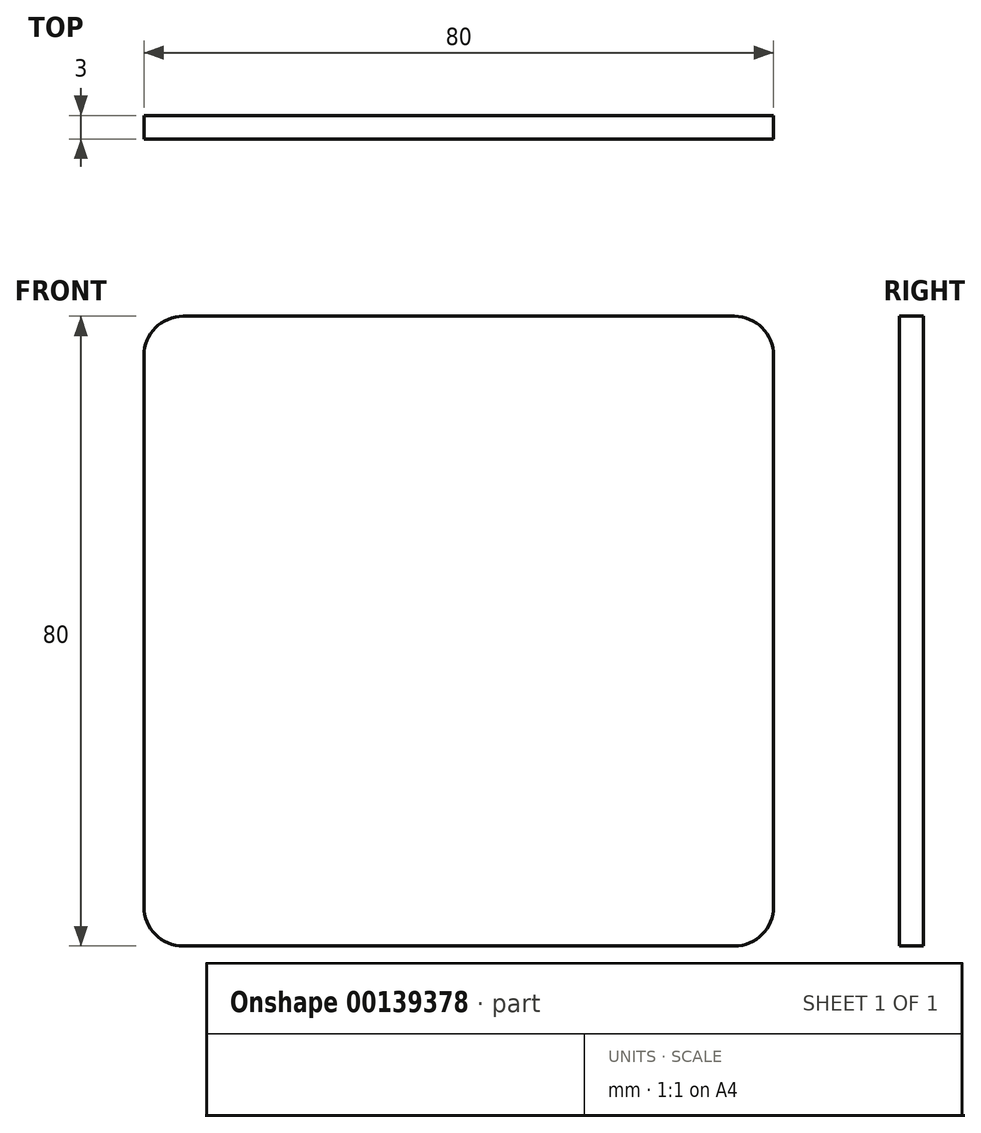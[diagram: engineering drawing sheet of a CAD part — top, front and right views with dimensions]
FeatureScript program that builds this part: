
annotation { "Feature Type Name" : "Feature", "Feature Type Description" : "" }
export const myFeature = defineFeature(function(context is Context, id is Id, definition is map)
    precondition{}
    {
        {
            var Q0;
            Q0=qCreatedBy(makeId("Front.planeOp"),FACE);
            var sketch = newSketch(context, id + "F0", { "sketchPlane" : qUnion([Q0])});
            skLineSegment(sketch, "E0.bottom", {"start": v(-5, 0) * mm, "end": v(-75, 0) * mm});
            skLineSegment(sketch, "E0.top", {"start": v(-5, 80) * mm, "end": v(-75, 80) * mm});
            skLineSegment(sketch, "E0.left", {"start": v(0, 5) * mm, "end": v(0, 75) * mm});
            skLineSegment(sketch, "E0.right", {"start": v(-80, 5) * mm, "end": v(-80, 75) * mm});
            skPoint(sketch, "E1.visualSharp", {"position": v(-80, 80) * mm});
            skArc(sketch, "E1.filletArc", {"start": v(-75, 80) * mm, "mid": v(-78.54, 78.54) * mm, "end": v(-80, 75) * mm});
            skPoint(sketch, "E2.visualSharp", {"position": v(0, 80) * mm});
            skArc(sketch, "E2.filletArc", {"start": v(0, 75) * mm, "mid": v(-1.46, 78.54) * mm, "end": v(-5, 80) * mm});
            skPoint(sketch, "E3.visualSharp", {"position": v(0, 0) * mm});
            skArc(sketch, "E3.filletArc", {"start": v(-5, 0) * mm, "mid": v(-1.46, 1.46) * mm, "end": v(0, 5) * mm});
            skPoint(sketch, "E4.visualSharp", {"position": v(-80, 0) * mm});
            skArc(sketch, "E4.filletArc", {"start": v(-80, 5) * mm, "mid": v(-78.54, 1.46) * mm, "end": v(-75, 0) * mm});
            skSolve(sketch);
        }
        {
            var Q0;
            Q0 = qSketchRegion(id + "F0", true);
            extrude(context, id + "F1", {"entities" : qUnion([Q0]), "depth" : 3 * mm});
        }
    });
